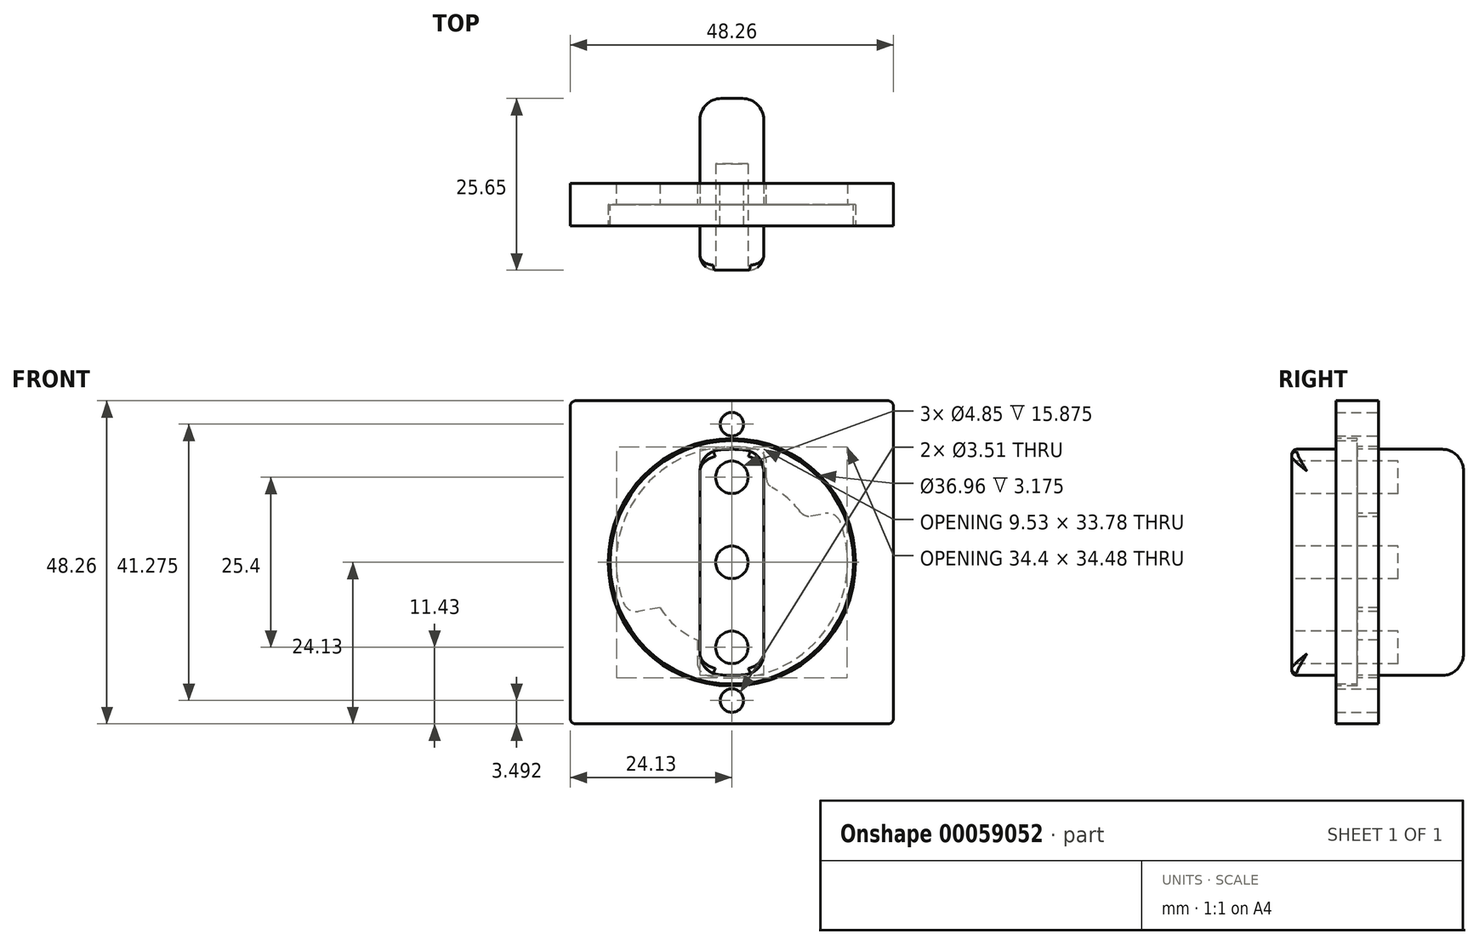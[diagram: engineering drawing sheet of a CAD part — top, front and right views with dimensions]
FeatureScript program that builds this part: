
annotation { "Feature Type Name" : "Feature", "Feature Type Description" : "" }
export const myFeature = defineFeature(function(context is Context, id is Id, definition is map)
    precondition{}
    {
        {
            var Q0;
            Q0=qCreatedBy(makeId("Front.planeOp"),FACE);
            var sketch = newSketch(context, id + "F0", { "sketchPlane" : qUnion([Q0])});
            skLineSegment(sketch, "E0.bottom", {"start": v(23.34, -24.13) * mm, "end": v(-23.34, -24.13) * mm});
            skLineSegment(sketch, "E0.top", {"start": v(23.34, 24.13) * mm, "end": v(-23.34, 24.13) * mm});
            skLineSegment(sketch, "E0.left", {"start": v(24.13, -23.34) * mm, "end": v(24.13, 23.34) * mm});
            skLineSegment(sketch, "E0.right", {"start": v(-24.13, -23.34) * mm, "end": v(-24.13, 23.34) * mm});
            skPoint(sketch, "E0.middle", {"position": v(0, 0) * mm});
            skPoint(sketch, "E1.visualSharp", {"position": v(-24.13, 24.13) * mm});
            skArc(sketch, "E1.filletArc", {"start": v(-23.34, 24.13) * mm, "mid": v(-23.9, 23.9) * mm, "end": v(-24.13, 23.34) * mm});
            skPoint(sketch, "E2.visualSharp", {"position": v(24.13, 24.13) * mm});
            skArc(sketch, "E2.filletArc", {"start": v(24.13, 23.34) * mm, "mid": v(23.9, 23.9) * mm, "end": v(23.34, 24.13) * mm});
            skPoint(sketch, "E3.visualSharp", {"position": v(24.13, -24.13) * mm});
            skArc(sketch, "E3.filletArc", {"start": v(23.34, -24.13) * mm, "mid": v(23.9, -23.9) * mm, "end": v(24.13, -23.34) * mm});
            skPoint(sketch, "E4.visualSharp", {"position": v(-24.13, -24.13) * mm});
            skArc(sketch, "E4.filletArc", {"start": v(-24.13, -23.34) * mm, "mid": v(-23.9, -23.9) * mm, "end": v(-23.34, -24.13) * mm});
            skCircle(sketch, "E5", {"center": v(0, 0) * mm, "radius": 12.7 * mm});
            skSolve(sketch);
        }
        {
            var Q0;
            Q0 = qSketchRegion(id + "F0", true);
            extrude(context, id + "F1", {"entities" : qUnion([Q0]), "depth" : 6.35 * mm});
        }
        {
            var Q0;
            Q0=makeQuery(id+"F1.opExtrude","CAP_FACE",FACE,{"disambiguationData":[OSD([sQuery(id+"F0.wireOp",EDGE,"E0.bottom"),sQuery(id+"F0.wireOp",EDGE,"E0.top"),sQuery(id+"F0.wireOp",EDGE,"E0.left"),sQuery(id+"F0.wireOp",EDGE,"E0.right"),sQuery(id+"F0.wireOp",EDGE,"E1.filletArc"),sQuery(id+"F0.wireOp",EDGE,"E2.filletArc"),sQuery(id+"F0.wireOp",EDGE,"E3.filletArc"),sQuery(id+"F0.wireOp",EDGE,"E4.filletArc")])],"isStart":false});
            var sketch = newSketch(context, id + "F2", { "sketchPlane" : qUnion([Q0])});
            skArc(sketch, "E6", {"start": v(5.14, 16.49) * mm, "mid": v(-13.1, 11.25) * mm, "end": v(-15.51, -7.6) * mm});
            skArc(sketch, "E7", {"start": v(-5.14, -16.49) * mm, "mid": v(13.1, -11.25) * mm, "end": v(15.51, 7.6) * mm});
            skLineSegment(sketch, "E8", {"start": v(5.14, 16.49) * mm, "end": v(5.14, 11.61) * mm});
            skLineSegment(sketch, "E9", {"start": v(-5.14, -16.49) * mm, "end": v(-5.14, -11.61) * mm});
            skLineSegment(sketch, "E10", {"start": v(-15.51, -7.6) * mm, "end": v(-10.76, -6.75) * mm});
            skLineSegment(sketch, "E11", {"start": v(15.51, 7.6) * mm, "end": v(10.76, 6.75) * mm});
            skLineSegment(sketch, "E12", {"start": v(0, 0) * mm, "end": v(-30.64, 0) * mm, "construction": true});
            skLineSegment(sketch, "E13", {"start": v(5.14, 16.49) * mm, "end": v(15.51, 7.6) * mm, "construction": true});
            skLineSegment(sketch, "E14", {"start": v(-15.51, -7.6) * mm, "end": v(-5.14, -16.49) * mm, "construction": true});
            skSolve(sketch);
        }
        {
            var Q0;
            Q0=makeQuery(id+"F2.imprint","IMPRINT",FACE,{"disambiguationData":[TD([[makeQuery(id+"F2.imprint","IMPRINT",EDGE,{"derivedFrom":sQuery(id+"F2.wireOp",EDGE,"E6")}),1.0]])]});
            var Q1;
            Q1=makeQuery(id+"F2.imprint","IMPRINT",FACE,{"disambiguationData":[TD([[makeQuery(id+"F2.imprint","IMPRINT",EDGE,{"derivedFrom":sQuery(id+"F2.wireOp",EDGE,"E7")}),1.0]])]});
            extrude(context, id + "F3", {"entities" : qUnion([Q0, Q1]), "operationType" : NewBodyOperationType.REMOVE, "endBound" : BoundingType.THROUGH_ALL, "oppositeDirection" : true, "depth" : 25.4 * mm});
        }
        {
            var Q0;
            Q0=makeQuery(id+"F3.boolean.opBoolean","COPY",EDGE,{"derivedFrom":makeQuery(id+"F3.opExtrude","SWEPT_EDGE",EDGE,{"disambiguationData":[OSD([sQuery(id+"F2.wireOp",EDGE,"E6"),sQuery(id+"F2.wireOp",EDGE,"E8")])]})});
            var Q1;
            Q1=makeQuery(id+"F3.boolean.opBoolean","COPY",EDGE,{"derivedFrom":makeQuery(id+"F3.opExtrude","SWEPT_EDGE",EDGE,{"disambiguationData":[OSD([sQuery(id+"F2.wireOp",EDGE,"E7"),sQuery(id+"F2.wireOp",EDGE,"E11")])]})});
            var Q2;
            Q2=makeQuery(id+"F3.boolean.opBoolean","COPY",EDGE,{"derivedFrom":makeQuery(id+"F3.opExtrude","SWEPT_EDGE",EDGE,{"disambiguationData":[OSD([sQuery(id+"F2.wireOp",EDGE,"E7"),sQuery(id+"F2.wireOp",EDGE,"E9")])]})});
            var Q3;
            Q3=makeQuery(id+"F3.boolean.opBoolean","COPY",EDGE,{"derivedFrom":makeQuery(id+"F3.opExtrude","SWEPT_EDGE",EDGE,{"disambiguationData":[OSD([sQuery(id+"F2.wireOp",EDGE,"E6"),sQuery(id+"F2.wireOp",EDGE,"E10")])]})});
            fillet(context, id + "F4", {"entities" : qUnion([Q0, Q1, Q2, Q3]), "radius" : 1.98 * mm, "tangentPropagation" : true, "allowEdgeOverflow" : false});
        }
        {
            var Q0;
            Q0=makeQuery(id+"F3.boolean.opBoolean","COPY",EDGE,{"derivedFrom":makeQuery(id+"F3.opExtrude","SWEPT_EDGE",EDGE,{"disambiguationData":[OSD([sQuery(id+"F0.wireOp",EDGE,"E5"),sQuery(id+"F2.wireOp",EDGE,"E9")])]})});
            var Q1;
            Q1=makeQuery(id+"F3.boolean.opBoolean","COPY",EDGE,{"derivedFrom":makeQuery(id+"F3.opExtrude","SWEPT_EDGE",EDGE,{"disambiguationData":[OSD([sQuery(id+"F0.wireOp",EDGE,"E5"),sQuery(id+"F2.wireOp",EDGE,"E10")])]})});
            var Q2;
            Q2=makeQuery(id+"F3.boolean.opBoolean","COPY",EDGE,{"derivedFrom":makeQuery(id+"F3.opExtrude","SWEPT_EDGE",EDGE,{"disambiguationData":[OSD([sQuery(id+"F0.wireOp",EDGE,"E5"),sQuery(id+"F2.wireOp",EDGE,"E11")])]})});
            var Q3;
            Q3=makeQuery(id+"F3.boolean.opBoolean","COPY",EDGE,{"derivedFrom":makeQuery(id+"F3.opExtrude","SWEPT_EDGE",EDGE,{"disambiguationData":[OSD([sQuery(id+"F0.wireOp",EDGE,"E5"),sQuery(id+"F2.wireOp",EDGE,"E8")])]})});
            fillet(context, id + "F5", {"entities" : qUnion([Q0, Q1, Q2, Q3]), "radius" : 1.59 * mm, "tangentPropagation" : true, "allowEdgeOverflow" : false});
        }
        {
            var Q0;
            Q0=makeQuery(id+"F1.opExtrude","CAP_FACE",FACE,{"disambiguationData":[OSD([sQuery(id+"F0.wireOp",EDGE,"E0.bottom"),sQuery(id+"F0.wireOp",EDGE,"E0.top"),sQuery(id+"F0.wireOp",EDGE,"E0.left"),sQuery(id+"F0.wireOp",EDGE,"E0.right"),sQuery(id+"F0.wireOp",EDGE,"E1.filletArc"),sQuery(id+"F0.wireOp",EDGE,"E2.filletArc"),sQuery(id+"F0.wireOp",EDGE,"E3.filletArc"),sQuery(id+"F0.wireOp",EDGE,"E4.filletArc"),sQuery(id+"F0.wireOp",EDGE,"E5")])],"isStart":false});
            var sketch = newSketch(context, id + "F6", { "sketchPlane" : qUnion([Q0])});
            skCircle(sketch, "E15", {"center": v(0, 0) * mm, "radius": 18.48 * mm});
            skSolve(sketch);
        }
        {
            var Q0;
            Q0 = qSketchRegion(id + "F6", true);
            extrude(context, id + "F7", {"entities" : qUnion([Q0]), "operationType" : NewBodyOperationType.REMOVE, "oppositeDirection" : true, "depth" : 3.17 * mm});
        }
        {
            var Q0;
            Q0=makeQuery(id+"F1.opExtrude","CAP_FACE",FACE,{"disambiguationData":[OSD([sQuery(id+"F0.wireOp",EDGE,"E0.bottom"),sQuery(id+"F0.wireOp",EDGE,"E0.top"),sQuery(id+"F0.wireOp",EDGE,"E0.left"),sQuery(id+"F0.wireOp",EDGE,"E0.right"),sQuery(id+"F0.wireOp",EDGE,"E1.filletArc"),sQuery(id+"F0.wireOp",EDGE,"E2.filletArc"),sQuery(id+"F0.wireOp",EDGE,"E3.filletArc"),sQuery(id+"F0.wireOp",EDGE,"E4.filletArc"),sQuery(id+"F0.wireOp",EDGE,"E5")])],"isStart":true});
            var sketch = newSketch(context, id + "F8", { "sketchPlane" : qUnion([Q0])});
            skPoint(sketch, "E16", {"position": v(0, 20.64) * mm});
            skPoint(sketch, "E17", {"position": v(0, -20.64) * mm});
            skLineSegment(sketch, "E18", {"start": v(0, -20.64) * mm, "end": v(0, 0) * mm, "construction": true});
            skLineSegment(sketch, "E19", {"start": v(0, 0) * mm, "end": v(0, 20.64) * mm, "construction": true});
            skSolve(sketch);
        }
        {
            var Q0;
            Q0=sQuery(id+"F8.wireOp",VERTEX,"E16");
            var Q1;
            Q1=sQuery(id+"F8.wireOp",VERTEX,"E18.start");
            var Q2;
            Q2=makeQuery(id+"F1.opExtrude","SWEPT_BODY",BODY,{"disambiguationData":[OSD([sQuery(id+"F0.wireOp",EDGE,"E0.bottom"),sQuery(id+"F0.wireOp",EDGE,"E0.top"),sQuery(id+"F0.wireOp",EDGE,"E0.left"),sQuery(id+"F0.wireOp",EDGE,"E0.right"),sQuery(id+"F0.wireOp",EDGE,"E1.filletArc"),sQuery(id+"F0.wireOp",EDGE,"E2.filletArc"),sQuery(id+"F0.wireOp",EDGE,"E3.filletArc"),sQuery(id+"F0.wireOp",EDGE,"E4.filletArc"),sQuery(id+"F0.wireOp",EDGE,"E5")])]});
            hole(context, id + "F9", {"style" : HoleStyle.SIMPLE, "endStyle" : HoleEndStyle.THROUGH, "holeDiameter" : 3.5 * mm, "startFromSketch" : true, "locations" : qUnion([Q0, Q1]), "scope" : qUnion([Q2]), "isTappedThrough" : true});
        }
        {
            var Q0;
            Q0=makeQuery(id+"F7.boolean.opBoolean","COPY",FACE,{"derivedFrom":makeQuery(id+"F7.opExtrude","CAP_FACE",FACE,{"disambiguationData":[OSD([sQuery(id+"F6.wireOp",EDGE,"E15")])],"isStart":false})});
            var sketch = newSketch(context, id + "F10", { "sketchPlane" : qUnion([Q0])});
            skCircle(sketch, "E20", {"center": v(0, 0) * mm, "radius": 18.16 * mm});
            skSolve(sketch);
        }
        {
            var Q0;
            Q0 = qSketchRegion(id + "F10", true);
            extrude(context, id + "F11", {"entities" : qUnion([Q0]), "depth" : 3.17 * mm});
        }
        {
            var Q0;
            Q0=makeQuery(id+"F11.opExtrude","CAP_FACE",FACE,{"disambiguationData":[OSD([sQuery(id+"F10.wireOp",EDGE,"E20")])],"isStart":true});
            var sketch = newSketch(context, id + "F12", { "sketchPlane" : qUnion([Q0])});
            skLineSegment(sketch, "E21.left", {"start": v(-4.76, 13.62) * mm, "end": v(-4.76, -13.62) * mm});
            skLineSegment(sketch, "E21.right", {"start": v(4.76, 13.62) * mm, "end": v(4.76, -13.62) * mm});
            skPoint(sketch, "E21.middle", {"position": v(0, 0) * mm});
            skArc(sketch, "E22", {"start": v(1.95, 16.78) * mm, "mid": v(0, 16.9) * mm, "end": v(-1.95, 16.78) * mm});
            skArc(sketch, "E23", {"start": v(-1.95, -16.78) * mm, "mid": v(0, -16.9) * mm, "end": v(1.95, -16.78) * mm});
            skPoint(sketch, "E24.visualSharp", {"position": v(-4.76, 16.2) * mm});
            skArc(sketch, "E24.filletArc", {"start": v(-1.95, 16.78) * mm, "mid": v(-3.96, 15.73) * mm, "end": v(-4.76, 13.62) * mm});
            skPoint(sketch, "E25.visualSharp", {"position": v(4.76, 16.2) * mm});
            skArc(sketch, "E25.filletArc", {"start": v(4.76, 13.62) * mm, "mid": v(3.96, 15.73) * mm, "end": v(1.95, 16.78) * mm});
            skPoint(sketch, "E26.visualSharp", {"position": v(4.76, -16.2) * mm});
            skArc(sketch, "E26.filletArc", {"start": v(1.95, -16.78) * mm, "mid": v(3.96, -15.73) * mm, "end": v(4.76, -13.62) * mm});
            skPoint(sketch, "E27.visualSharp", {"position": v(-4.76, -16.2) * mm});
            skArc(sketch, "E27.filletArc", {"start": v(-4.76, -13.62) * mm, "mid": v(-3.96, -15.73) * mm, "end": v(-1.95, -16.78) * mm});
            skSolve(sketch);
        }
        {
            var Q0;
            Q0 = qSketchRegion(id + "F12", true);
            extrude(context, id + "F13", {"entities" : qUnion([Q0]), "operationType" : NewBodyOperationType.ADD, "depth" : 15.88 * mm});
        }
        {
            var Q0;
            Q0=makeQuery(id+"F13.opExtrude","CAP_FACE",FACE,{"disambiguationData":[OSD([sQuery(id+"F12.wireOp",EDGE,"E21.left"),sQuery(id+"F12.wireOp",EDGE,"E21.right"),sQuery(id+"F12.wireOp",EDGE,"E22"),sQuery(id+"F12.wireOp",EDGE,"E23"),sQuery(id+"F12.wireOp",EDGE,"E24.filletArc"),sQuery(id+"F12.wireOp",EDGE,"E25.filletArc"),sQuery(id+"F12.wireOp",EDGE,"E26.filletArc"),sQuery(id+"F12.wireOp",EDGE,"E27.filletArc")])],"isStart":false});
            fillet(context, id + "F14", {"entities" : qUnion([Q0]), "radius" : 3.17 * mm, "tangentPropagation" : true, "allowEdgeOverflow" : false});
        }
        {
            var Q0;
            Q0=makeQuery(id+"F11.opExtrude","CAP_FACE",FACE,{"disambiguationData":[OSD([sQuery(id+"F10.wireOp",EDGE,"E20")])],"isStart":false});
            var sketch = newSketch(context, id + "F15", { "sketchPlane" : qUnion([Q0])});
            skLineSegment(sketch, "E28.0", {"start": v(4.76, 13.62) * mm, "end": v(4.76, -13.62) * mm});
            skArc(sketch, "E28.1", {"start": v(4.76, -13.62) * mm, "mid": v(3.96, -15.73) * mm, "end": v(1.95, -16.78) * mm});
            skArc(sketch, "E28.2", {"start": v(1.95, -16.78) * mm, "mid": v(0, -16.9) * mm, "end": v(-1.95, -16.78) * mm});
            skArc(sketch, "E28.3", {"start": v(-1.95, -16.78) * mm, "mid": v(-3.96, -15.73) * mm, "end": v(-4.76, -13.62) * mm});
            skLineSegment(sketch, "E28.4", {"start": v(-4.76, 13.62) * mm, "end": v(-4.76, -13.62) * mm});
            skArc(sketch, "E28.5", {"start": v(-4.76, 13.62) * mm, "mid": v(-3.96, 15.73) * mm, "end": v(-1.95, 16.78) * mm});
            skPoint(sketch, "E28.6", {"position": v(1.95, 16.78) * mm});
            skArc(sketch, "E28.7", {"start": v(-1.95, 16.78) * mm, "mid": v(0, 16.9) * mm, "end": v(1.95, 16.78) * mm});
            skArc(sketch, "E28.8", {"start": v(1.95, 16.78) * mm, "mid": v(3.96, 15.73) * mm, "end": v(4.76, 13.62) * mm});
            skPoint(sketch, "E28.9", {"position": v(-3.96, 15.73) * mm});
            skPoint(sketch, "E28.10", {"position": v(0, 16.9) * mm});
            skSolve(sketch);
        }
        {
            var Q0;
            Q0 = qSketchRegion(id + "F15", true);
            extrude(context, id + "F16", {"entities" : qUnion([Q0]), "operationType" : NewBodyOperationType.ADD, "depth" : 6.6 * mm});
        }
        {
            var Q0;
            Q0=makeQuery(id+"F16.opExtrude","CAP_EDGE",EDGE,{"disambiguationData":[OSD([sQuery(id+"F15.wireOp",EDGE,"E28.4")])],"isStart":false});
            var Q1;
            Q1=makeQuery(id+"F16.opExtrude","CAP_EDGE",EDGE,{"disambiguationData":[OSD([sQuery(id+"F15.wireOp",EDGE,"E28.0")])],"isStart":false});
            fillet(context, id + "F17", {"entities" : qUnion([Q0, Q1]), "radius" : 2.3 * mm, "allowEdgeOverflow" : false});
        }
        {
            var Q0;
            Q0=makeQuery(id+"F16.opExtrude","CAP_FACE",FACE,{"disambiguationData":[OSD([sQuery(id+"F15.wireOp",EDGE,"E28.0"),sQuery(id+"F15.wireOp",EDGE,"E28.1"),sQuery(id+"F15.wireOp",EDGE,"E28.2"),sQuery(id+"F15.wireOp",EDGE,"E28.3"),sQuery(id+"F15.wireOp",EDGE,"E28.4"),sQuery(id+"F15.wireOp",EDGE,"E28.5"),sQuery(id+"F15.wireOp",EDGE,"E28.7"),sQuery(id+"F15.wireOp",EDGE,"E28.8")])],"isStart":false});
            var sketch = newSketch(context, id + "F18", { "sketchPlane" : qUnion([Q0])});
            skCircle(sketch, "E29", {"center": v(0, 0) * mm, "radius": 2.43 * mm});
            skCircle(sketch, "E30", {"center": v(0, 12.7) * mm, "radius": 2.43 * mm});
            skCircle(sketch, "E31", {"center": v(0, -12.7) * mm, "radius": 2.43 * mm});
            skSolve(sketch);
        }
        {
            var Q0;
            Q0 = qSketchRegion(id + "F18", true);
            extrude(context, id + "F19", {"entities" : qUnion([Q0]), "operationType" : NewBodyOperationType.REMOVE, "oppositeDirection" : true, "depth" : 15.88 * mm});
        }
        {
            var Q0;
            Q0=makeQuery(id+"F16.opExtrude","CAP_EDGE",EDGE,{"disambiguationData":[OSD([sQuery(id+"F15.wireOp",EDGE,"E28.7")])],"isStart":false});
            var Q1;
            Q1=makeQuery(id+"F16.opExtrude","CAP_EDGE",EDGE,{"disambiguationData":[OSD([sQuery(id+"F15.wireOp",EDGE,"E28.2")])],"isStart":false});
            fillet(context, id + "F20", {"entities" : qUnion([Q0, Q1]), "radius" : 0.8 * mm, "tangentPropagation" : true, "allowEdgeOverflow" : false});
        }
    });
